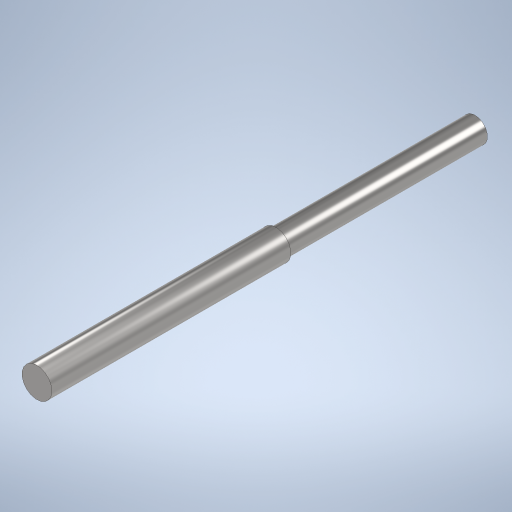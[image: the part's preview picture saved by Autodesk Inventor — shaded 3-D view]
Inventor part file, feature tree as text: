
AUTODESK INVENTOR PART (.ipt)
format: ipt  version: 2023 (Build 270158000, 158)  size: 264,192 bytes
history: native  units: mm
features: extrude x3, sketch x3
ambient origin geometry x8: Origin, YZ Plane, XZ Plane, XY Plane, X Axis, Y Axis, Z Axis, Center Point
bodies: Solid1 (feature_tree)
feature tree (6):
  extrude  "Extrusion1"  Depth=4.0mm TaperAngle=0.0deg
  extrude  "Extrusion2"  Depth=20.0mm TaperAngle=0.0deg
  extrude  "Extrusion3"  Depth=20.0mm TaperAngle=0.0deg
  sketch  "Sketch1"  dims[d0=3.0mm d1=4.0mm d2=0.0mm]
  sketch  "Sketch2"  dims[d3=3.0mm d4=20.0mm d5=0.0mm]
  sketch  "Sketch3"  dims[d8=2.5mm d9=20.0mm d10=0.0mm]
